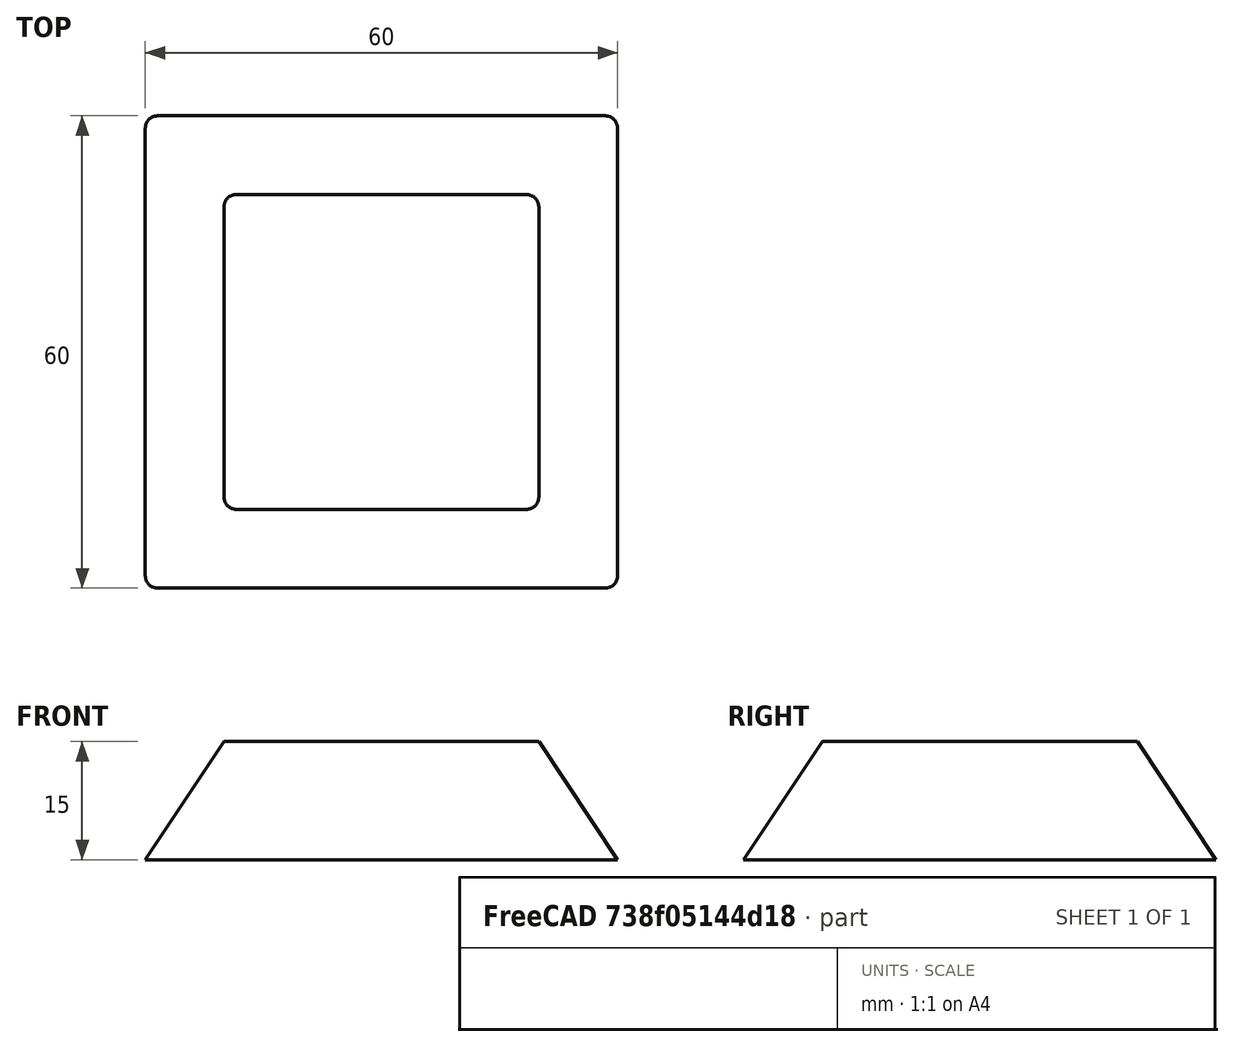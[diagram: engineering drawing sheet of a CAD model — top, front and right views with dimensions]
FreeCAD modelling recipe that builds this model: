
FCSTD DOCUMENT  (FreeCAD 0.18R16131 (Git))
Label: bac-perles
License: All rights reserved
LicenseURL: http://en.wikipedia.org/wiki/All_rights_reserved
objects: PartDesign::AdditiveWedge×1, PartDesign::Fillet×1, PartDesign::Body×1
note: 4 computed .brp shape members not serialized (recipe doc carries the construction recipe); baked Part::Feature solids carry a one-line shape summary decoded from their .brp

FEATURE [PartDesign::AdditiveWedge] Wedge
  AttacherType = Attacher::AttachEngine3D
  MapMode = 2
  Placement = pos=(0,0,0) rot=(0.57735,0.57735,0.57735;2.0944rad)
  Support = -> [Y_Axis]
  X2max = 50
  X2min = 10
  Xmax = 60
  Xmin = 0
  Ymax = 15
  Ymin = 0
  Z2max = 50
  Z2min = 10
  Zmax = 60
  Zmin = 0
FEATURE [PartDesign::Fillet] Fillet
  Base = -> Wedge [Edge8,Edge6,Edge2,Edge4]
  BaseFeature = -> Wedge
  Placement = pos=(0,0,0) rot=(0.57735,0.57735,0.57735;2.0944rad)
  Radius = 2
FEATURE [PartDesign::Body] Body
  Group = -> [Wedge,Fillet]
  Origin = -> Origin
  Tip = -> Fillet
